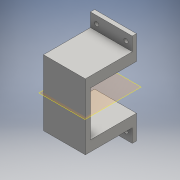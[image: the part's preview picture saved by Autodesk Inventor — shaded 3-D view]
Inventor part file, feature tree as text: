
AUTODESK INVENTOR PART (.ipt)
format: ipt  version: 2016 (Build 200138000, 138)  size: 142,848 bytes
history: native  units: mm
features: extrude x4, sketch x4, mirror x1
ambient origin geometry x8: Origin, YZ Plane, XZ Plane, XY Plane, X Axis, Y Axis, Z Axis, Center Point
bodies: Solid1 (feature_tree)
feature tree (9):
  extrude  "Extrusion1"  Depth=62.91mm
  extrude  "Extrusion2"  Depth=10.0mm
  extrude  "Extrusion3"  Depth=0.012774mm
  extrude  "Extrusion5"  Depth=43.91mm TaperAngle=0.0deg
  mirror  "Mirror1"
  sketch  "Sketch1"  dims[d0=40.0mm d1=62.91mm]
  sketch  "Sketch2"  dims[d2=5.0mm d3=0.0mm d4=10.0mm]
  sketch  "Sketch3"  dims[d5=10.0mm d6=0.012774mm]
  sketch  "Sketch5"  dims[d7=40.0mm d8=43.91mm d9=0.0mm d10=4.0mm d11=13.0mm d12=0.0mm d17=4.0mm d18=4.0mm d19=6.0mm d20=6.0mm d21=6.0mm d22=20.0mm d23=0.0mm]
